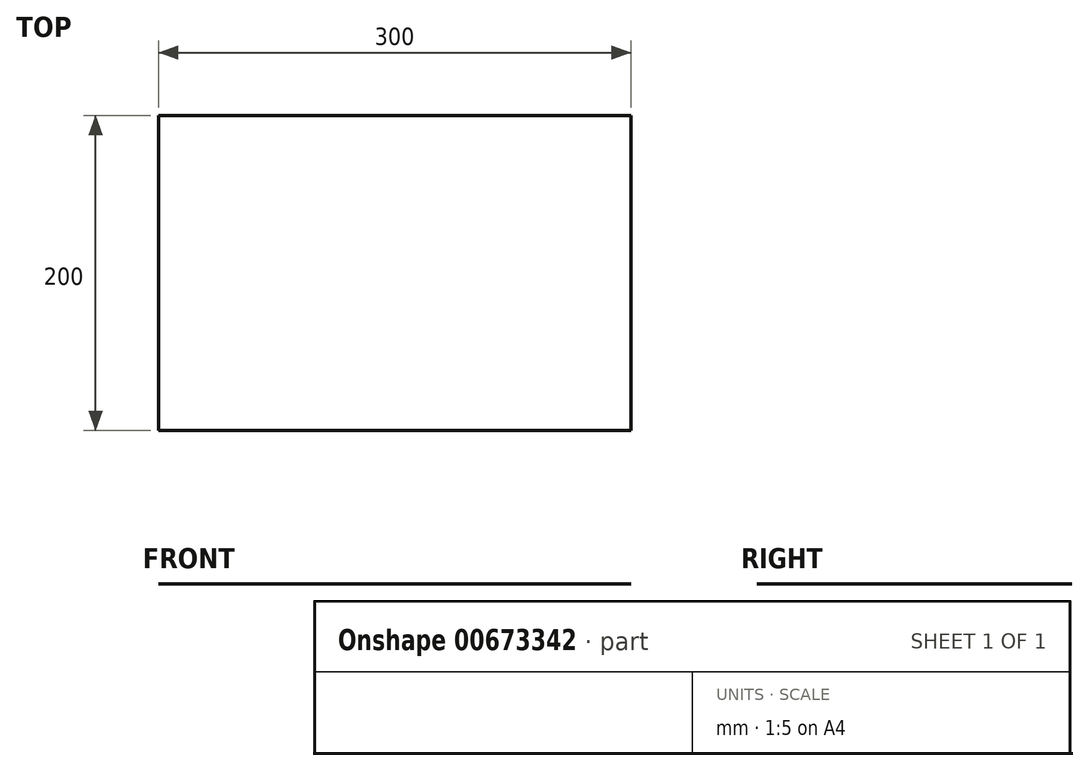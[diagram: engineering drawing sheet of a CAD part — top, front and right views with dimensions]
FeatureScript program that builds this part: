
annotation { "Feature Type Name" : "Feature", "Feature Type Description" : "" }
export const myFeature = defineFeature(function(context is Context, id is Id, definition is map)
    precondition{}
    {
        {
            var Q0;
            Q0=qCreatedBy(makeId("Top.planeOp"),FACE);
            var sketch = newSketch(context, id + "F0", { "sketchPlane" : qUnion([Q0])});
            skLineSegment(sketch, "E0.bottom", {"start": v(-145.92, 36.38) * mm, "end": v(154.08, 36.38) * mm});
            skLineSegment(sketch, "E0.top", {"start": v(-145.92, -163.62) * mm, "end": v(154.08, -163.62) * mm});
            skLineSegment(sketch, "E0.left", {"start": v(-145.92, 36.38) * mm, "end": v(-145.92, -163.62) * mm});
            skLineSegment(sketch, "E0.right", {"start": v(154.08, 36.38) * mm, "end": v(154.08, -163.62) * mm});
            skLineSegment(sketch, "E1", {"start": v(-145.92, 36.38) * mm, "end": v(154.08, -163.62) * mm});
            skSolve(sketch);
        }
        {
            var Q0;
            Q0 = qSketchRegion(id + "F0", true);
            extrude(context, id + "F1", {"entities" : qUnion([Q0]), "endBound" : BoundingType.SYMMETRIC, "depth" : 1 / 101.6 * mm, "offsetDistance" : 25 * mm});
        }
    });
